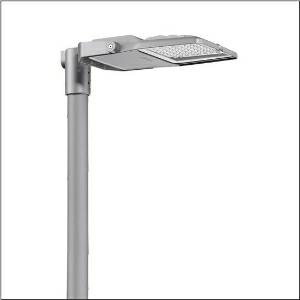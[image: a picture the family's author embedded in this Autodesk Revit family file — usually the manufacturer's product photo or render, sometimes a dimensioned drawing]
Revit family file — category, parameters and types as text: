
# Revit family: floodlight_fl_21_mini___pl64_5xa7776d4e3a_3ee3
name_source: partatom
category: Lighting Fixtures
units: mm (PartAtom-declared; Revit-internal decimal feet)

## family parameters
Cut with Voids When Loaded = No
Host = Face
Light Source = No
Part Type = Normal
Room Calculation Point = No
Round Connector Dimension = Use Diameter
Shared = No

## types (1)
- --- (1 x LED, 17960 lm, 142.9 W, 4000K)
    Apparent Load = 143 VA
    CIE Flux Codes = 28 80 98 100 100
    Color Rendering = 70
    Color Temperature = 4000K
    Default Elevation = 1800 mm
    Description = Floodlight FL 21 mini, floodlight, primary light control with lens, of PMMA, primary optical cover: protective disc, of toughened safety glass, transparent, light distribution: PL64, light emission: direct distribution, installation type: surface-mounted, LED, High Power LED, rated luminous flux: 17.960lm, luminous efficacy: 126lm/W, light colour: 740, colour temperature: 4000K, control gear: D4iSmart Interface (Zhaga), control: overheat protection, constant luminous flux control, time-dependent luminous flux control, flexible luminous flux parameterisation, pre-setting: logarithmic dimming characteristic, with terminal, 6-pole, mains connection: 220..240V, AC, 50/60Hz, start of lifetime: 143W, end of service life: 151W, reduction: 63W, mast bracket, of diecast aluminium, powder-coated, SITECO metallic grey (DB 702S), corrosivity category C5 mid according to DIN EN ISO 12944, suitable for swimming pools, chlorine-resistant, sealing non-destructively replaceable, mast bracket, of steel, galvanised, powder-coated, SITECO metallic grey (DB 702S), Smart Interface below and above, protection rating (complete): IP66, insulation class (complete): insulation class II (safety insulation), certification: CE, ENEC, VDE, protection symbol: D, impact resistance: IK08, permissible operating ambient temperature: -40..+40°C, permissible operating ambient temperature for outdoor applications: -40..+50°C, standard: DIN EN 12944, LABS conformity tested according to VDMA 24364:2018-05, packaging unit: 1 piece

Light Distribution: PL64
    Height = 70 mm
    Lamp = 1 x LED
    Lamp Light Flux = 17960 lm
    Lamp Power = 142.9 W
    Lamp count = 1
    Length = 485 mm
    Luminous efficacy = 126 lm/W
    Manufacturer = Siteco
    ModVariant = No
    Model = 5XA7776D4E3A
    Number of Poles = 1
    OnlyDefault = Yes
    Power Factor = 1
    Product Name = Floodlight FL 21 mini | PL64
    Product group = floodlight | pylon annexe
    ProductGroupID = 6201
    Protection Class = Protection class II
    Protection Degree = IP 66
    RLX_Detail_Level = 1
    RLX_Emergency_Light_Flux = 0 lm
    RLX_Emergency_Type = 0
    RLX_Emergency_Type_DB = No
    RlxData = <blob elided: 101221 chars, md5=f0ec054a>
    Socket = socket
    Standby Power = 0 W
    System Light Flux = 17960 lm
    System Power = 143 W
    Type Comments = factory setting: luminous flux: 100 % | dim-lin: 254 | 730 mA
    Type Image = l_1007125.jpg
    URL = http://relux.com
    VarID = @adj_099939
    Voltage = 0 V
    Weight = 0.00 kg
    Width = 337 mm

## geometry (parser evidence)
native form markers: Blend x4, Sweep x14
no freeform markers — native parametric forms only
